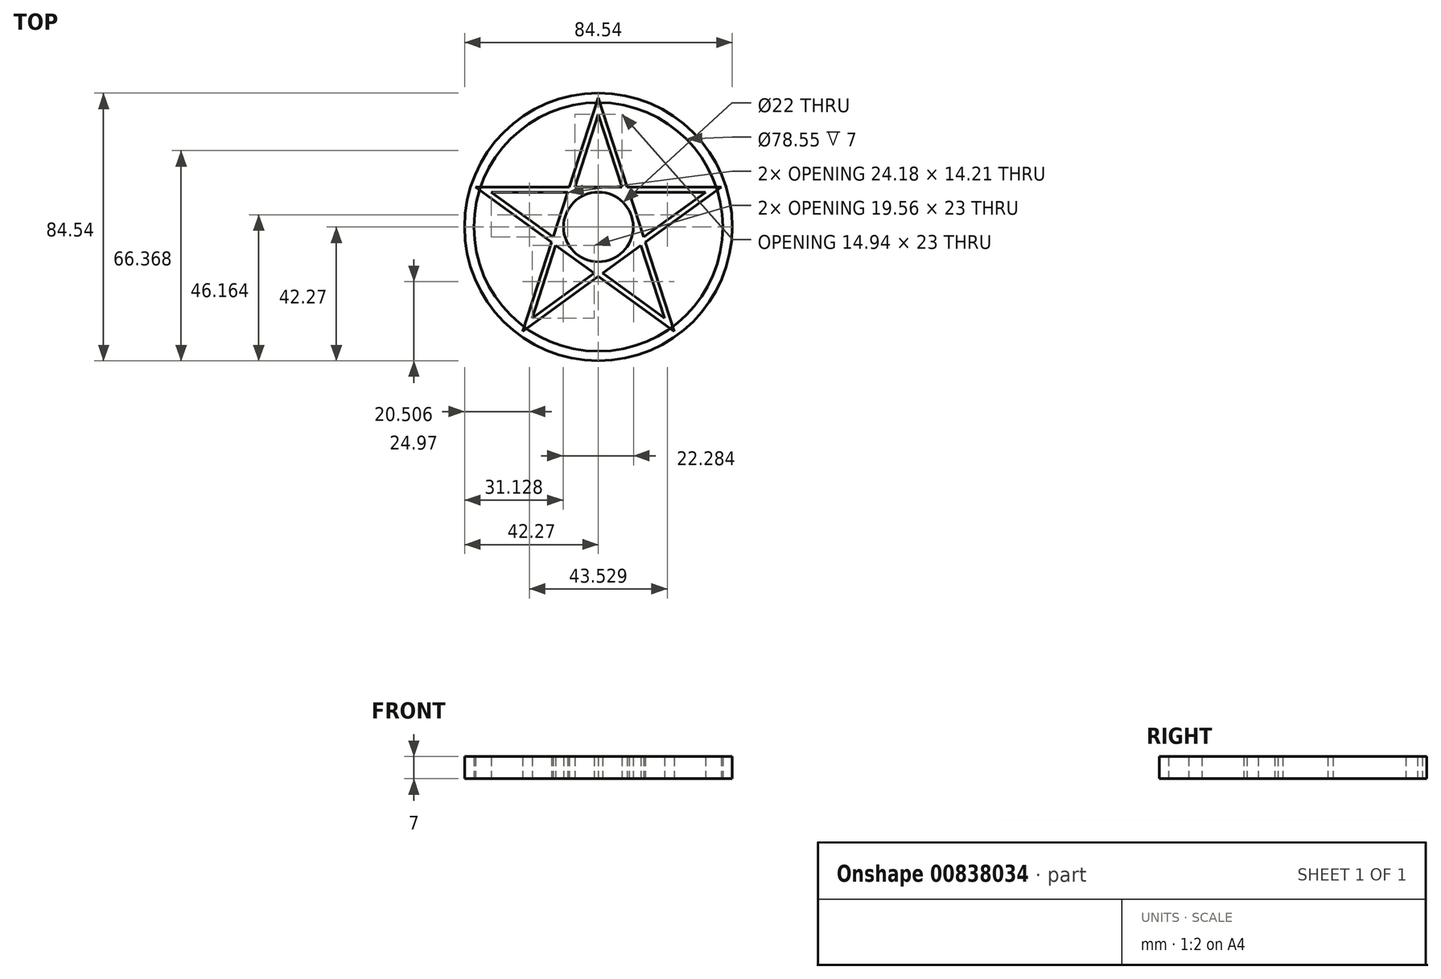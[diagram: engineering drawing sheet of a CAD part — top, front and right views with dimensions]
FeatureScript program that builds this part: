
annotation { "Feature Type Name" : "Feature", "Feature Type Description" : "" }
export const myFeature = defineFeature(function(context is Context, id is Id, definition is map)
    precondition{}
    {
        {
            var Q0;
            Q0=qCreatedBy(makeId("Top.planeOp"),FACE);
            var sketch = newSketch(context, id + "F0", { "sketchPlane" : qUnion([Q0])});
            skCircle(sketch, "E0.cCircle", {"center": v(0, 0) * mm, "radius": 32.99 * mm, "construction": true});
            skLineSegment(sketch, "E0.0", {"start": v(0, 40.77) * mm, "end": v(38.78, 12.6) * mm, "construction": true});
            skLineSegment(sketch, "E0.1", {"start": v(38.78, 12.6) * mm, "end": v(23.97, -32.99) * mm, "construction": true});
            skLineSegment(sketch, "E0.2", {"start": v(23.97, -32.99) * mm, "end": v(-23.97, -32.99) * mm, "construction": true});
            skLineSegment(sketch, "E0.3", {"start": v(-23.97, -32.99) * mm, "end": v(-38.78, 12.6) * mm, "construction": true});
            skLineSegment(sketch, "E0.4", {"start": v(-38.78, 12.6) * mm, "end": v(0, 40.77) * mm, "construction": true});
            skPoint(sketch, "E0.0.midPoint", {"position": v(19.39, 26.69) * mm});
            skLineSegment(sketch, "E1", {"start": v(-23.97, -32.99) * mm, "end": v(0, 40.77) * mm});
            skLineSegment(sketch, "E2", {"start": v(0, 40.77) * mm, "end": v(23.97, -32.99) * mm});
            skLineSegment(sketch, "E3", {"start": v(23.97, -32.99) * mm, "end": v(-38.78, 12.6) * mm});
            skLineSegment(sketch, "E4", {"start": v(-38.78, 12.6) * mm, "end": v(38.78, 12.6) * mm});
            skLineSegment(sketch, "E5", {"start": v(38.78, 12.6) * mm, "end": v(-23.97, -32.99) * mm});
            skCircle(sketch, "E6", {"center": v(0, 0) * mm, "radius": 11 * mm});
            skCircle(sketch, "E7.cCircle", {"center": v(0, 0) * mm, "radius": 28.8 * mm, "construction": true});
            skLineSegment(sketch, "E7.0", {"start": v(0, 35.6) * mm, "end": v(33.85, 11) * mm, "construction": true});
            skLineSegment(sketch, "E7.1", {"start": v(33.85, 11) * mm, "end": v(20.92, -28.8) * mm, "construction": true});
            skLineSegment(sketch, "E7.2", {"start": v(20.92, -28.8) * mm, "end": v(-20.92, -28.8) * mm, "construction": true});
            skLineSegment(sketch, "E7.3", {"start": v(-20.92, -28.8) * mm, "end": v(-33.85, 11) * mm, "construction": true});
            skLineSegment(sketch, "E7.4", {"start": v(-33.85, 11) * mm, "end": v(0, 35.6) * mm, "construction": true});
            skLineSegment(sketch, "E8", {"start": v(-20.92, -28.8) * mm, "end": v(0, 35.6) * mm});
            skLineSegment(sketch, "E9", {"start": v(20.92, -28.8) * mm, "end": v(0, 35.6) * mm});
            skLineSegment(sketch, "E10", {"start": v(20.92, -28.8) * mm, "end": v(-33.85, 11) * mm});
            skLineSegment(sketch, "E11", {"start": v(-33.85, 11) * mm, "end": v(33.85, 11) * mm});
            skLineSegment(sketch, "E12", {"start": v(33.85, 11) * mm, "end": v(-20.92, -28.8) * mm});
            skSolve(sketch);
        }
        {
            var Q0;
            Q0=qCreatedBy(makeId("Top.planeOp"),FACE);
            var sketch = newSketch(context, id + "F1", { "sketchPlane" : qUnion([Q0])});
            skCircle(sketch, "E13", {"center": v(0, 0) * mm, "radius": 40.77 * mm, "construction": true});
            skCircle(sketch, "E14", {"center": v(0, 0) * mm, "radius": 42.27 * mm});
            skLineSegment(sketch, "E15.0", {"start": v(38.78, 12.6) * mm, "end": v(-23.97, -32.99) * mm, "construction": true});
            skCircle(sketch, "E16", {"center": v(0, 0) * mm, "radius": 39.27 * mm});
            skSolve(sketch);
        }
        {
            var Q0;
            {var subQ0=sQuery(id+"F0.wireOp",EDGE,"E3");var subQ1=sQuery(id+"F0.wireOp",EDGE,"E1");var subQ2=makeQuery(id+"F0.imprint","INTERSECT",VERTEX,{"derivedFrom":[subQ1,subQ0]});Q0=makeQuery(id+"F0.imprint","IMPRINT",FACE,{"disambiguationData":[TD([[makeQuery(id+"F0.imprint","IMPRINT",EDGE,{"disambiguationData":[TD([[subQ2,-1.0]])],"derivedFrom":subQ1}),1.0]])]});}
            var Q1;
            {var subQ0=sQuery(id+"F0.wireOp",EDGE,"E2");var subQ1=sQuery(id+"F0.wireOp",EDGE,"E1");var subQ2=makeQuery(id+"F0.imprint","INTERSECT",VERTEX,{"derivedFrom":[subQ1,subQ0]});Q1=makeQuery(id+"F0.imprint","IMPRINT",FACE,{"disambiguationData":[TD([[makeQuery(id+"F0.imprint","IMPRINT",EDGE,{"disambiguationData":[TD([[subQ2,1.0]])],"derivedFrom":subQ1}),-1.0]])]});}
            var Q2;
            {var subQ0=sQuery(id+"F0.wireOp",EDGE,"E4");var subQ1=sQuery(id+"F0.wireOp",EDGE,"E2");var subQ2=makeQuery(id+"F0.imprint","INTERSECT",VERTEX,{"derivedFrom":[subQ1,subQ0]});Q2=makeQuery(id+"F0.imprint","IMPRINT",FACE,{"disambiguationData":[TD([[makeQuery(id+"F0.imprint","IMPRINT",EDGE,{"disambiguationData":[TD([[subQ2,-1.0]])],"derivedFrom":subQ1}),1.0]])]});}
            var Q3;
            {var subQ1=sQuery(id+"F0.wireOp",EDGE,"E1");var subQ5=sQuery(id+"F0.wireOp",EDGE,"E3");var subQ6=makeQuery(id+"F0.imprint","INTERSECT",VERTEX,{"derivedFrom":[subQ1,subQ5]});Q3=makeQuery(id+"F0.imprint","IMPRINT",FACE,{"disambiguationData":[TD([[makeQuery(id+"F0.imprint","IMPRINT",EDGE,{"disambiguationData":[TD([[subQ6,-1.0]])],"derivedFrom":subQ1}),-1.0]])]});}
            var Q4;
            {var subQ0=sQuery(id+"F0.wireOp",EDGE,"E3");var subQ1=sQuery(id+"F0.wireOp",EDGE,"E2");var subQ2=makeQuery(id+"F0.imprint","INTERSECT",VERTEX,{"derivedFrom":[subQ1,subQ0]});Q4=makeQuery(id+"F0.imprint","IMPRINT",FACE,{"disambiguationData":[TD([[makeQuery(id+"F0.imprint","IMPRINT",EDGE,{"disambiguationData":[TD([[subQ2,1.0]])],"derivedFrom":subQ1}),-1.0]])]});}
            var Q5;
            {var subQ0=sQuery(id+"F0.wireOp",EDGE,"E5");var subQ1=sQuery(id+"F0.wireOp",EDGE,"E1");var subQ2=makeQuery(id+"F0.imprint","INTERSECT",VERTEX,{"derivedFrom":[subQ1,subQ0]});Q5=makeQuery(id+"F0.imprint","IMPRINT",FACE,{"disambiguationData":[TD([[makeQuery(id+"F0.imprint","IMPRINT",EDGE,{"disambiguationData":[TD([[subQ2,-1.0]])],"derivedFrom":subQ1}),-1.0]])]});}
            var Q6;
            {var subQ4=sQuery(id+"F0.wireOp",EDGE,"E12");var subQ5=sQuery(id+"F0.wireOp",EDGE,"E3");var subQ6=makeQuery(id+"F0.imprint","INTERSECT",VERTEX,{"derivedFrom":[subQ5,subQ4]});Q6=makeQuery(id+"F0.imprint","IMPRINT",FACE,{"disambiguationData":[TD([[makeQuery(id+"F0.imprint","IMPRINT",EDGE,{"disambiguationData":[TD([[subQ6,-1.0]])],"derivedFrom":subQ5}),-1.0]])]});}
            var Q7;
            {var subQ0=sQuery(id+"F0.wireOp",EDGE,"E5");var subQ1=sQuery(id+"F0.wireOp",EDGE,"E2");var subQ2=makeQuery(id+"F0.imprint","INTERSECT",VERTEX,{"derivedFrom":[subQ1,subQ0]});Q7=makeQuery(id+"F0.imprint","IMPRINT",FACE,{"disambiguationData":[TD([[makeQuery(id+"F0.imprint","IMPRINT",EDGE,{"disambiguationData":[TD([[subQ2,1.0]])],"derivedFrom":subQ1}),-1.0]])]});}
            var Q8;
            {var subQ0=sQuery(id+"F0.wireOp",EDGE,"E4");var subQ1=sQuery(id+"F0.wireOp",EDGE,"E2");var subQ2=makeQuery(id+"F0.imprint","INTERSECT",VERTEX,{"derivedFrom":[subQ1,subQ0]});Q8=makeQuery(id+"F0.imprint","IMPRINT",FACE,{"disambiguationData":[TD([[makeQuery(id+"F0.imprint","IMPRINT",EDGE,{"disambiguationData":[TD([[subQ2,-1.0]])],"derivedFrom":subQ1}),-1.0]])]});}
            var Q9;
            {var subQ0=sQuery(id+"F0.wireOp",EDGE,"E4");var subQ1=sQuery(id+"F0.wireOp",EDGE,"E1");var subQ2=makeQuery(id+"F0.imprint","INTERSECT",VERTEX,{"derivedFrom":[subQ1,subQ0]});Q9=makeQuery(id+"F0.imprint","IMPRINT",FACE,{"disambiguationData":[TD([[makeQuery(id+"F0.imprint","IMPRINT",EDGE,{"disambiguationData":[TD([[subQ2,1.0]])],"derivedFrom":subQ1}),-1.0]])]});}
            var Q10;
            {var subQ2=sQuery(id+"F0.wireOp",EDGE,"E8");var subQ4=sQuery(id+"F0.wireOp",EDGE,"E4");var subQ5=makeQuery(id+"F0.imprint","INTERSECT",VERTEX,{"derivedFrom":[subQ4,subQ2]});Q10=makeQuery(id+"F0.imprint","IMPRINT",FACE,{"disambiguationData":[TD([[makeQuery(id+"F0.imprint","IMPRINT",EDGE,{"disambiguationData":[TD([[subQ5,-1.0]])],"derivedFrom":subQ4}),-1.0]])]});}
            var Q11;
            {var subQ0=sQuery(id+"F0.wireOp",EDGE,"E10");var subQ1=sQuery(id+"F0.wireOp",EDGE,"E1");var subQ2=makeQuery(id+"F0.imprint","INTERSECT",VERTEX,{"derivedFrom":[subQ1,subQ0]});Q11=makeQuery(id+"F0.imprint","IMPRINT",FACE,{"disambiguationData":[TD([[makeQuery(id+"F0.imprint","IMPRINT",EDGE,{"disambiguationData":[TD([[subQ2,-1.0]])],"derivedFrom":subQ1}),-1.0]])]});}
            var Q12;
            {var subQ2=sQuery(id+"F0.wireOp",EDGE,"E9");var subQ5=sQuery(id+"F0.wireOp",EDGE,"E5");var subQ8=makeQuery(id+"F0.imprint","INTERSECT",VERTEX,{"derivedFrom":[subQ5,subQ2]});Q12=makeQuery(id+"F0.imprint","IMPRINT",FACE,{"disambiguationData":[TD([[makeQuery(id+"F0.imprint","IMPRINT",EDGE,{"disambiguationData":[TD([[subQ8,-1.0]])],"derivedFrom":subQ5}),-1.0]])]});}
            var Q13;
            {var subQ2=sQuery(id+"F0.wireOp",EDGE,"E11");var subQ6=sQuery(id+"F0.wireOp",EDGE,"E2");var subQ7=makeQuery(id+"F0.imprint","INTERSECT",VERTEX,{"derivedFrom":[subQ6,subQ2]});Q13=makeQuery(id+"F0.imprint","IMPRINT",FACE,{"disambiguationData":[TD([[makeQuery(id+"F0.imprint","IMPRINT",EDGE,{"disambiguationData":[TD([[subQ7,-1.0]])],"derivedFrom":subQ6}),-1.0]])]});}
            var Q14;
            {var subQ0=sQuery(id+"F0.wireOp",EDGE,"E5");var subQ1=sQuery(id+"F0.wireOp",EDGE,"E3");var subQ2=makeQuery(id+"F0.imprint","INTERSECT",VERTEX,{"derivedFrom":[subQ1,subQ0]});Q14=makeQuery(id+"F0.imprint","IMPRINT",FACE,{"disambiguationData":[TD([[makeQuery(id+"F0.imprint","IMPRINT",EDGE,{"disambiguationData":[TD([[subQ2,-1.0]])],"derivedFrom":subQ1}),-1.0]])]});}
            var Q15;
            {var subQ0=sQuery(id+"F0.wireOp",EDGE,"E8");var subQ1=sQuery(id+"F0.wireOp",EDGE,"E6");var subQ2=makeQuery(id+"F0.imprint","INTERSECT",VERTEX,{"derivedFrom":[subQ1,subQ0]});Q15=makeQuery(id+"F0.imprint","IMPRINT",FACE,{"disambiguationData":[TD([[makeQuery(id+"F0.imprint","IMPRINT",EDGE,{"disambiguationData":[TD([[subQ2,-1.0]])],"derivedFrom":subQ1}),-1.0]])]});}
            var Q16;
            {var subQ0=sQuery(id+"F0.wireOp",EDGE,"E10");var subQ1=sQuery(id+"F0.wireOp",EDGE,"E6");var subQ2=makeQuery(id+"F0.imprint","INTERSECT",VERTEX,{"derivedFrom":[subQ1,subQ0]});Q16=makeQuery(id+"F0.imprint","IMPRINT",FACE,{"disambiguationData":[TD([[makeQuery(id+"F0.imprint","IMPRINT",EDGE,{"disambiguationData":[TD([[subQ2,-1.0]])],"derivedFrom":subQ1}),-1.0]])]});}
            var Q17;
            {var subQ0=sQuery(id+"F0.wireOp",EDGE,"E9");var subQ1=sQuery(id+"F0.wireOp",EDGE,"E6");var subQ2=makeQuery(id+"F0.imprint","INTERSECT",VERTEX,{"derivedFrom":[subQ1,subQ0]});Q17=makeQuery(id+"F0.imprint","IMPRINT",FACE,{"disambiguationData":[TD([[makeQuery(id+"F0.imprint","IMPRINT",EDGE,{"disambiguationData":[TD([[subQ2,1.0]])],"derivedFrom":subQ1}),-1.0]])]});}
            var Q18;
            {var subQ0=sQuery(id+"F0.wireOp",EDGE,"E11");var subQ1=sQuery(id+"F0.wireOp",EDGE,"E6");var subQ2=makeQuery(id+"F0.imprint","INTERSECT",VERTEX,{"derivedFrom":[subQ1,subQ0]});Q18=makeQuery(id+"F0.imprint","IMPRINT",FACE,{"disambiguationData":[TD([[makeQuery(id+"F0.imprint","IMPRINT",EDGE,{"disambiguationData":[TD([[subQ2,1.0]])],"derivedFrom":subQ1}),-1.0]])]});}
            var Q19;
            {var subQ0=sQuery(id+"F0.wireOp",EDGE,"E11");var subQ1=sQuery(id+"F0.wireOp",EDGE,"E6");var subQ2=makeQuery(id+"F0.imprint","INTERSECT",VERTEX,{"derivedFrom":[subQ1,subQ0]});Q19=makeQuery(id+"F0.imprint","IMPRINT",FACE,{"disambiguationData":[TD([[makeQuery(id+"F0.imprint","IMPRINT",EDGE,{"disambiguationData":[TD([[subQ2,-1.0]])],"derivedFrom":subQ1}),-1.0]])]});}
            var Q20;
            Q20=makeQuery(id+"F1.imprint","IMPRINT",FACE,{"disambiguationData":[TD([[makeQuery(id+"F1.imprint","IMPRINT",EDGE,{"derivedFrom":sQuery(id+"F1.wireOp",EDGE,"E14")}),1.0]])]});
            extrude(context, id + "F2", {"entities" : qUnion([Q0, Q1, Q2, Q3, Q4, Q5, Q6, Q7, Q8, Q9, Q10, Q11, Q12, Q13, Q14, Q15, Q16, Q17, Q18, Q19, Q20]), "depth" : 7 * mm, "offsetDistance" : 25 * mm});
        }
    });
